# Revit family: Diffuser-Carnes-Ducted_Plenum-CXPC
name_source: partatom
category: Duct Accessories
revit_build: Autodesk Revit MEP 2014 (Build: 20130308_1515(x64)
units: mm (PartAtom-declared; Revit-internal decimal feet)

## types (1)
- Parametric
    A = 10 1/2"
    B = 60"
    B Radius = 63"
    Catalog = http://www.carnes.com
    Default Elevation = 0"
    Depth = 2 3/4"
    Description = Widebody Diffuser
    Half Inlet Width = 2 1/2"
    Height = 9 1/16"
    Inlet Nominal Size Height D = 3 1/2"
    Inlet Nominal Size Width = 5"
    Length = 23 1/2"
    Manufacturer = CARNES COMPANY
    Model = CXPC Ducted Plenum
    Product Page URL = http://www.carnes.com
    Revit Object Download Link = http://library.smartbim.com
    Slot Width = 1 75/128"
    Specification Sheet = http://www.carnes.com
    Subcatagory = Linear Diffuser
    Supply Connection = Diffuser Supply Connector
    Supply Connector = No
    URL = http://www.carnes.com
    Unit = Metal - Carnes - Steel Galvanized

## geometry (parser evidence)
native form markers: Blend x2, Sweep x5
no freeform markers — native parametric forms only
